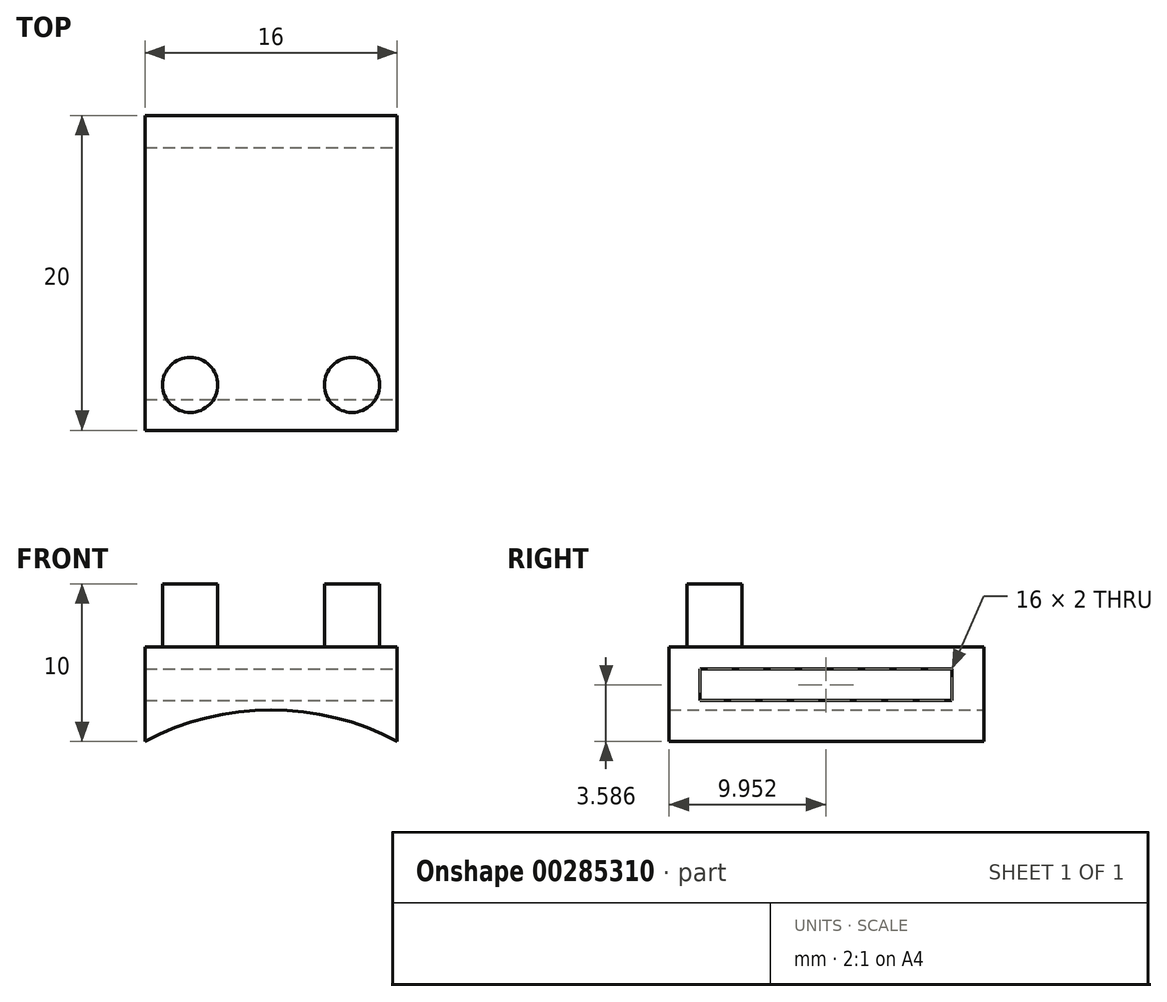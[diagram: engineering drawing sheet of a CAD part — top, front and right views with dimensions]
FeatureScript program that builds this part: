
annotation { "Feature Type Name" : "Feature", "Feature Type Description" : "" }
export const myFeature = defineFeature(function(context is Context, id is Id, definition is map)
    precondition{}
    {
        {
            var Q0;
            Q0=qCreatedBy(makeId("Front.planeOp"),FACE);
            var sketch = newSketch(context, id + "F0", { "sketchPlane" : qUnion([Q0])});
            skLineSegment(sketch, "E0.rect.bottom", {"start": v(8, -3.7) * mm, "end": v(-8, -3.7) * mm});
            skLineSegment(sketch, "E0.rect.top", {"start": v(8, 2.3) * mm, "end": v(-8, 2.3) * mm});
            skLineSegment(sketch, "E0.rect.left", {"start": v(8, -3.7) * mm, "end": v(8, 2.3) * mm});
            skLineSegment(sketch, "E0.rect.right", {"start": v(-8, -3.7) * mm, "end": v(-8, 2.3) * mm});
            skPoint(sketch, "E0.rect.middle", {"position": v(0, 0) * mm});
            skArc(sketch, "E1", {"start": v(8, -3.7) * mm, "mid": v(0, -1.7) * mm, "end": v(-8, -3.7) * mm});
            skPoint(sketch, "E2", {"position": v(0, -1.7) * mm});
            skPoint(sketch, "E3", {"position": v(0, -3.7) * mm});
            skSolve(sketch);
        }
        {
            var Q0;
            Q0=makeQuery(id+"F0.imprint","IMPRINT",FACE,{"disambiguationData":[TD([[makeQuery(id+"F0.imprint","IMPRINT",EDGE,{"derivedFrom":sQuery(id+"F0.wireOp",EDGE,"E0.rect.top")}),1.0]])]});
            extrude(context, id + "F1", {"entities" : qUnion([Q0]), "depth" : 20 * mm});
        }
        {
            var Q0;
            Q0=makeQuery(id+"F1.opExtrude","SWEPT_FACE",FACE,{"disambiguationData":[OSD([sQuery(id+"F0.wireOp",EDGE,"E0.rect.left")])]});
            var sketch = newSketch(context, id + "F2", { "sketchPlane" : qUnion([Q0])});
            skLineSegment(sketch, "E4.bottom", {"start": v(-18.05, 0.89) * mm, "end": v(-2.05, 0.89) * mm});
            skLineSegment(sketch, "E4.top", {"start": v(-18.05, -1.11) * mm, "end": v(-2.05, -1.11) * mm});
            skLineSegment(sketch, "E4.left", {"start": v(-18.05, 0.89) * mm, "end": v(-18.05, -1.11) * mm});
            skLineSegment(sketch, "E4.right", {"start": v(-2.05, 0.89) * mm, "end": v(-2.05, -1.11) * mm});
            skSolve(sketch);
        }
        {
            var Q0;
            Q0=makeQuery(id+"F2.imprint","IMPRINT",FACE,{"disambiguationData":[TD([[makeQuery(id+"F2.imprint","IMPRINT",EDGE,{"derivedFrom":sQuery(id+"F2.wireOp",EDGE,"E4.bottom")}),-1.0]])]});
            extrude(context, id + "F3", {"entities" : qUnion([Q0]), "operationType" : NewBodyOperationType.REMOVE, "endBound" : BoundingType.UP_TO_NEXT, "oppositeDirection" : true, "depth" : 16 * mm});
        }
        {
            var Q0;
            Q0=makeQuery(id+"F1.opExtrude","SWEPT_FACE",FACE,{"disambiguationData":[OSD([sQuery(id+"F0.wireOp",EDGE,"E0.rect.top")])]});
            var sketch = newSketch(context, id + "F4", { "sketchPlane" : qUnion([Q0])});
            skLineSegment(sketch, "E5", {"start": v(-8, -17.1) * mm, "end": v(8, -17.1) * mm, "construction": true});
            skLineSegment(sketch, "E6", {"start": v(-5.14, -20) * mm, "end": v(-5.14, 0) * mm, "construction": true});
            skLineSegment(sketch, "E7", {"start": v(5.14, -20) * mm, "end": v(5.14, 0) * mm, "construction": true});
            skLineSegment(sketch, "E8", {"start": v(5.14, 0) * mm, "end": v(-5.14, -20) * mm, "construction": true});
            skPoint(sketch, "E9", {"position": v(0, -10) * mm});
            skCircle(sketch, "E10", {"center": v(-5.14, -17.1) * mm, "radius": 1.75 * mm});
            skCircle(sketch, "E11", {"center": v(5.14, -17.1) * mm, "radius": 1.75 * mm});
            skSolve(sketch);
        }
        {
            var Q0;
            Q0=makeQuery(id+"F4.imprint","IMPRINT",FACE,{"disambiguationData":[TD([[makeQuery(id+"F4.imprint","IMPRINT",EDGE,{"derivedFrom":sQuery(id+"F4.wireOp",EDGE,"E10")}),1.0]])]});
            var Q1;
            Q1=makeQuery(id+"F4.imprint","IMPRINT",FACE,{"disambiguationData":[TD([[makeQuery(id+"F4.imprint","IMPRINT",EDGE,{"derivedFrom":sQuery(id+"F4.wireOp",EDGE,"E11")}),1.0]])]});
            var Q2;
            Q2=sQuery(id+"F4.wireOp",EDGE,"E10");
            var Q3;
            Q3=sQuery(id+"F4.wireOp",EDGE,"E11");
            extrude(context, id + "F5", {"entities" : qUnion([Q0, Q1]), "operationType" : NewBodyOperationType.ADD, "surfaceEntities" : qUnion([Q2, Q3]), "depth" : 4 * mm});
        }
    });
